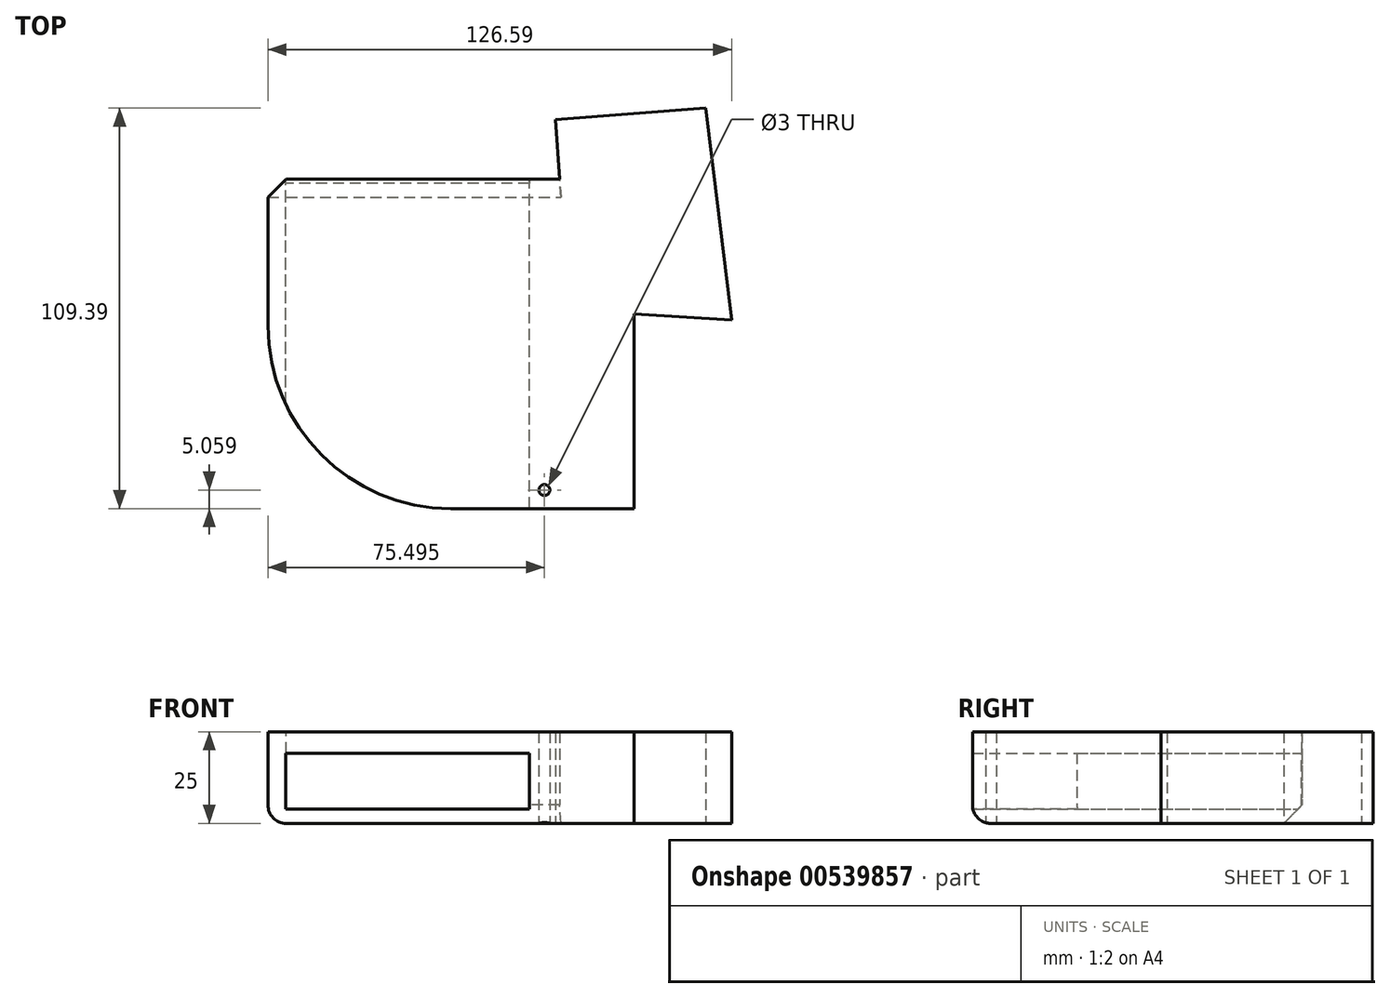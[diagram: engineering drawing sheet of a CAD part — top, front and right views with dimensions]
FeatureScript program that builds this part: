
annotation { "Feature Type Name" : "Feature", "Feature Type Description" : "" }
export const myFeature = defineFeature(function(context is Context, id is Id, definition is map)
    precondition{}
    {
        {
            var Q0;
            Q0=qCreatedBy(makeId("Top.planeOp"),FACE);
            var sketch = newSketch(context, id + "F0", { "sketchPlane" : qUnion([Q0])});
            skLineSegment(sketch, "E0.bottom", {"start": v(-50, 45) * mm, "end": v(29.66, 45) * mm});
            skLineSegment(sketch, "E0.top", {"start": v(0, -45) * mm, "end": v(50, -45) * mm});
            skLineSegment(sketch, "E0.left", {"start": v(-50, 45) * mm, "end": v(-50, 5) * mm});
            skLineSegment(sketch, "E0.right", {"start": v(50, 8.15) * mm, "end": v(50, -45) * mm});
            skCircle(sketch, "E1", {"center": v(25.5, -39.94) * mm, "radius": 1.5 * mm});
            skPoint(sketch, "E2.visualSharp", {"position": v(-50, -45) * mm});
            skArc(sketch, "E2.filletArc", {"start": v(-50, 5) * mm, "mid": v(-35.36, -30.36) * mm, "end": v(0, -45) * mm});
            skLineSegment(sketch, "E3", {"start": v(28.56, 61.21) * mm, "end": v(29.66, 45) * mm});
            skLineSegment(sketch, "E4", {"start": v(50, 8.15) * mm, "end": v(76.6, 6.46) * mm});
            skLineSegment(sketch, "E5", {"start": v(76.6, 6.46) * mm, "end": v(69.53, 64.4) * mm});
            skLineSegment(sketch, "E6", {"start": v(69.53, 64.4) * mm, "end": v(28.56, 61.21) * mm});
            skSolve(sketch);
        }
        {
            var Q0;
            Q0=makeQuery(id+"F0.imprint","IMPRINT",FACE,{"disambiguationData":[TD([[makeQuery(id+"F0.imprint","IMPRINT",EDGE,{"derivedFrom":sQuery(id+"F0.wireOp",EDGE,"E0.bottom")}),-1.0]])]});
            extrude(context, id + "F1", {"entities" : qUnion([Q0]), "depth" : 25 * mm, "offsetDistance" : 25 * mm});
        }
        {
            var Q0;
            Q0=makeQuery(id+"F1.opExtrude","SWEPT_FACE",FACE,{"disambiguationData":[OSD([sQuery(id+"F0.wireOp",EDGE,"E0.bottom")])]});
            var sketch = newSketch(context, id + "F2", { "sketchPlane" : qUnion([Q0])});
            skLineSegment(sketch, "E7.bottom", {"start": v(-21.37, 19.2) * mm, "end": v(45.13, 19.2) * mm});
            skLineSegment(sketch, "E7.top", {"start": v(-21.37, 3.87) * mm, "end": v(45.13, 3.87) * mm});
            skLineSegment(sketch, "E7.left", {"start": v(-21.37, 19.2) * mm, "end": v(-21.37, 3.87) * mm});
            skLineSegment(sketch, "E7.right", {"start": v(45.13, 19.2) * mm, "end": v(45.13, 3.87) * mm});
            skSolve(sketch);
        }
        {
            var Q0;
            Q0=makeQuery(id+"F2.imprint","IMPRINT",FACE,{"disambiguationData":[TD([[makeQuery(id+"F2.imprint","IMPRINT",EDGE,{"derivedFrom":sQuery(id+"F2.wireOp",EDGE,"E7.bottom")}),-1.0]])]});
            extrude(context, id + "F3", {"entities" : qUnion([Q0]), "operationType" : NewBodyOperationType.REMOVE, "oppositeDirection" : true, "depth" : 120 * mm, "offsetDistance" : 25 * mm});
        }
        {
            var Q0;
            Q0=makeQuery(id+"F1.opExtrude","CAP_EDGE",EDGE,{"disambiguationData":[OSD([sQuery(id+"F0.wireOp",EDGE,"E0.left")])],"isStart":true});
            fillet(context, id + "F4", {"entities" : qUnion([Q0]), "radius" : 5 * mm, "tangentPropagation" : true, "allowEdgeOverflow" : false});
        }
        {
            var Q0;
            Q0=makeQuery(id+"F1.opExtrude","CAP_EDGE",EDGE,{"disambiguationData":[OSD([sQuery(id+"F0.wireOp",EDGE,"E0.bottom")])],"isStart":true});
            chamfer(context, id + "F5", {"entities" : qUnion([Q0]), "width" : 5 * mm, "tangentPropagation" : true});
        }
    });
